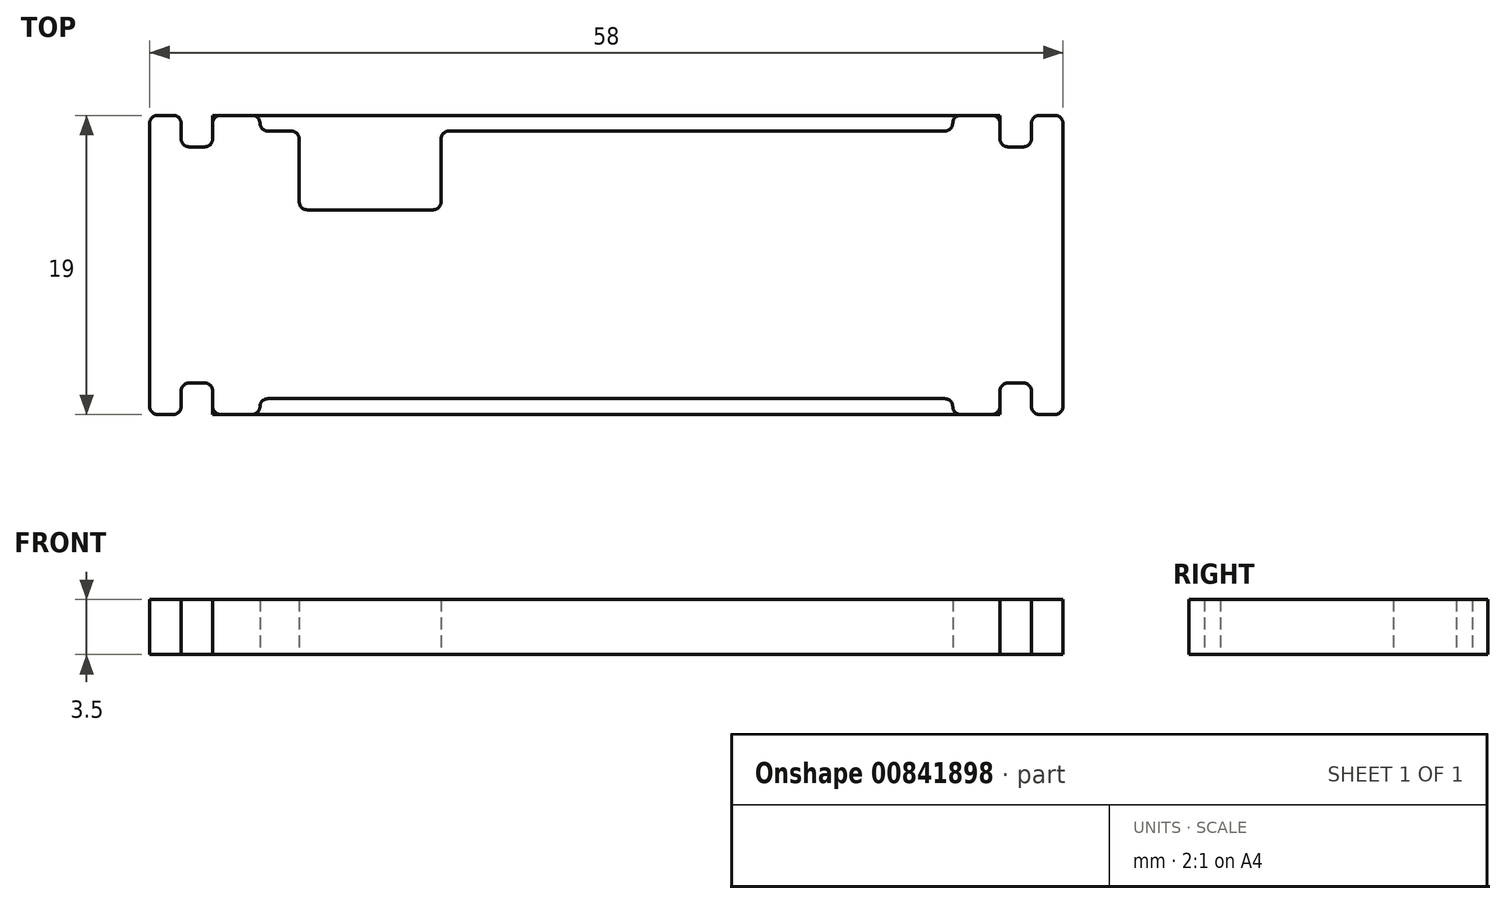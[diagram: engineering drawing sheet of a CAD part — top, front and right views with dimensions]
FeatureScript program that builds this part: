
annotation { "Feature Type Name" : "Feature", "Feature Type Description" : "" }
export const myFeature = defineFeature(function(context is Context, id is Id, definition is map)
    precondition{}
    {
        {
            var Q0;
            Q0=qCreatedBy(makeId("Top.planeOp"),FACE);
            var sketch = newSketch(context, id + "F0", { "sketchPlane" : qUnion([Q0])});
            skLineSegment(sketch, "E0", {"start": v(-28.5, 9.5) * mm, "end": v(-27.5, 9.5) * mm});
            skLineSegment(sketch, "E1", {"start": v(-27, 9) * mm, "end": v(-27, 8) * mm});
            skLineSegment(sketch, "E2", {"start": v(-26.5, 7.5) * mm, "end": v(-25.5, 7.5) * mm});
            skLineSegment(sketch, "E3", {"start": v(-25, 8) * mm, "end": v(-25, 9.5) * mm});
            skLineSegment(sketch, "E4", {"start": v(-25, 9.5) * mm, "end": v(0, 9.5) * mm});
            skLineSegment(sketch, "E5", {"start": v(-29, 9) * mm, "end": v(-29, 0) * mm});
            skLineSegment(sketch, "E6.MirrorCS", {"start": v(26.5, 7.5) * mm, "end": v(25.5, 7.5) * mm});
            skLineSegment(sketch, "E7.MirrorCS", {"start": v(28.5, 9.5) * mm, "end": v(27.5, 9.5) * mm});
            skLineSegment(sketch, "E8.MirrorCS", {"start": v(29, 9) * mm, "end": v(29, 0) * mm});
            skLineSegment(sketch, "E9.MirrorCS", {"start": v(25, 9.5) * mm, "end": v(0, 9.5) * mm});
            skLineSegment(sketch, "E10.MirrorCS", {"start": v(25, 8) * mm, "end": v(25, 9.5) * mm});
            skLineSegment(sketch, "E11.MirrorCS", {"start": v(27, 9) * mm, "end": v(27, 8) * mm});
            skLineSegment(sketch, "E12.MirrorCS", {"start": v(28.5, -9.5) * mm, "end": v(27.5, -9.5) * mm});
            skLineSegment(sketch, "E13.MirrorCS", {"start": v(-28.5, -9.5) * mm, "end": v(-27.5, -9.5) * mm});
            skLineSegment(sketch, "E14.MirrorCS", {"start": v(-26.5, -7.5) * mm, "end": v(-25.5, -7.5) * mm});
            skLineSegment(sketch, "E15.MirrorCS", {"start": v(26.5, -7.5) * mm, "end": v(25.5, -7.5) * mm});
            skLineSegment(sketch, "E16.MirrorCS", {"start": v(29, -9) * mm, "end": v(29, 0) * mm});
            skLineSegment(sketch, "E17.MirrorCS", {"start": v(-27, -9) * mm, "end": v(-27, -8) * mm});
            skLineSegment(sketch, "E18.MirrorCS", {"start": v(-29, -9) * mm, "end": v(-29, 0) * mm});
            skLineSegment(sketch, "E19.MirrorCS", {"start": v(27, -9) * mm, "end": v(27, -8) * mm});
            skLineSegment(sketch, "E20.MirrorCS", {"start": v(25, -8) * mm, "end": v(25, -9.5) * mm});
            skLineSegment(sketch, "E21.MirrorCS", {"start": v(25, -9.5) * mm, "end": v(0, -9.5) * mm});
            skLineSegment(sketch, "E22.MirrorCS", {"start": v(-25, -8) * mm, "end": v(-25, -9.5) * mm});
            skLineSegment(sketch, "E23.MirrorCS", {"start": v(-25, -9.5) * mm, "end": v(0, -9.5) * mm});
            skPoint(sketch, "E24.visualSharp", {"position": v(-29, 9.5) * mm});
            skArc(sketch, "E24.filletArc", {"start": v(-28.5, 9.5) * mm, "mid": v(-28.85, 9.35) * mm, "end": v(-29, 9) * mm});
            skPoint(sketch, "E25.visualSharp", {"position": v(-27, 9.5) * mm});
            skArc(sketch, "E25.filletArc", {"start": v(-27, 9) * mm, "mid": v(-27.15, 9.35) * mm, "end": v(-27.5, 9.5) * mm});
            skPoint(sketch, "E26.visualSharp", {"position": v(-27, 7.5) * mm});
            skArc(sketch, "E26.filletArc", {"start": v(-27, 8) * mm, "mid": v(-26.85, 7.65) * mm, "end": v(-26.5, 7.5) * mm});
            skPoint(sketch, "E27.visualSharp", {"position": v(-25, 7.5) * mm});
            skArc(sketch, "E27.filletArc", {"start": v(-25.5, 7.5) * mm, "mid": v(-25.15, 7.65) * mm, "end": v(-25, 8) * mm});
            skPoint(sketch, "E28.visualSharp", {"position": v(-29, -9.5) * mm});
            skArc(sketch, "E28.filletArc", {"start": v(-29, -9) * mm, "mid": v(-28.85, -9.35) * mm, "end": v(-28.5, -9.5) * mm});
            skPoint(sketch, "E29.visualSharp", {"position": v(-27, -9.5) * mm});
            skArc(sketch, "E29.filletArc", {"start": v(-27.5, -9.5) * mm, "mid": v(-27.15, -9.35) * mm, "end": v(-27, -9) * mm});
            skPoint(sketch, "E30.visualSharp", {"position": v(-27, -7.5) * mm});
            skArc(sketch, "E30.filletArc", {"start": v(-26.5, -7.5) * mm, "mid": v(-26.85, -7.65) * mm, "end": v(-27, -8) * mm});
            skPoint(sketch, "E31.visualSharp", {"position": v(-25, -7.5) * mm});
            skArc(sketch, "E31.filletArc", {"start": v(-25, -8) * mm, "mid": v(-25.15, -7.65) * mm, "end": v(-25.5, -7.5) * mm});
            skPoint(sketch, "E32.visualSharp", {"position": v(25, 7.5) * mm});
            skArc(sketch, "E32.filletArc", {"start": v(25, 8) * mm, "mid": v(25.15, 7.65) * mm, "end": v(25.5, 7.5) * mm});
            skPoint(sketch, "E33.visualSharp", {"position": v(27, 7.5) * mm});
            skArc(sketch, "E33.filletArc", {"start": v(26.5, 7.5) * mm, "mid": v(26.85, 7.65) * mm, "end": v(27, 8) * mm});
            skPoint(sketch, "E34.visualSharp", {"position": v(27, 9.5) * mm});
            skArc(sketch, "E34.filletArc", {"start": v(27.5, 9.5) * mm, "mid": v(27.15, 9.35) * mm, "end": v(27, 9) * mm});
            skPoint(sketch, "E35.visualSharp", {"position": v(29, 9.5) * mm});
            skArc(sketch, "E35.filletArc", {"start": v(29, 9) * mm, "mid": v(28.85, 9.35) * mm, "end": v(28.5, 9.5) * mm});
            skPoint(sketch, "E36.visualSharp", {"position": v(25, -7.5) * mm});
            skArc(sketch, "E36.filletArc", {"start": v(25.5, -7.5) * mm, "mid": v(25.15, -7.65) * mm, "end": v(25, -8) * mm});
            skPoint(sketch, "E37.visualSharp", {"position": v(27, -7.5) * mm});
            skArc(sketch, "E37.filletArc", {"start": v(27, -8) * mm, "mid": v(26.85, -7.65) * mm, "end": v(26.5, -7.5) * mm});
            skPoint(sketch, "E38.visualSharp", {"position": v(27, -9.5) * mm});
            skArc(sketch, "E38.filletArc", {"start": v(27, -9) * mm, "mid": v(27.15, -9.35) * mm, "end": v(27.5, -9.5) * mm});
            skPoint(sketch, "E39.visualSharp", {"position": v(29, -9.5) * mm});
            skArc(sketch, "E39.filletArc", {"start": v(28.5, -9.5) * mm, "mid": v(28.85, -9.35) * mm, "end": v(29, -9) * mm});
            skSolve(sketch);
        }
        {
            var Q0;
            Q0=qCreatedBy(makeId("Top.planeOp"),FACE);
            var sketch = newSketch(context, id + "F1", { "sketchPlane" : qUnion([Q0])});
            skLineSegment(sketch, "E40", {"start": v(-24.5, 9.5) * mm, "end": v(-22.5, 9.5) * mm});
            skLineSegment(sketch, "E41", {"start": v(-22, 9) * mm, "end": v(-22, 9) * mm});
            skLineSegment(sketch, "E42", {"start": v(-21.5, 8.5) * mm, "end": v(-20, 8.5) * mm});
            skLineSegment(sketch, "E43.MirrorCS", {"start": v(21.5, 8.5) * mm, "end": v(0, 8.5) * mm});
            skLineSegment(sketch, "E44.MirrorCS", {"start": v(22, 9) * mm, "end": v(22, 9) * mm});
            skLineSegment(sketch, "E45.MirrorCS", {"start": v(-24.5, -9.5) * mm, "end": v(-22.5, -9.5) * mm});
            skLineSegment(sketch, "E46.MirrorCS", {"start": v(-21.5, -8.5) * mm, "end": v(0, -8.5) * mm});
            skLineSegment(sketch, "E47.MirrorCS", {"start": v(21.5, -8.5) * mm, "end": v(0, -8.5) * mm});
            skLineSegment(sketch, "E48.MirrorCS", {"start": v(-22, -9) * mm, "end": v(-22, -9) * mm});
            skLineSegment(sketch, "E49.MirrorCS", {"start": v(22, -9) * mm, "end": v(22, -9) * mm});
            skPoint(sketch, "E50", {"position": v(-19.5, 8.5) * mm});
            skPoint(sketch, "E51", {"position": v(-10.5, 8.5) * mm});
            skLineSegment(sketch, "E52", {"start": v(-19.5, 8) * mm, "end": v(-19.5, 4) * mm});
            skLineSegment(sketch, "E53", {"start": v(-19, 3.5) * mm, "end": v(-11, 3.5) * mm});
            skLineSegment(sketch, "E54", {"start": v(-10.5, 4) * mm, "end": v(-10.5, 8) * mm});
            skLineSegment(sketch, "E55", {"start": v(-10, 8.5) * mm, "end": v(0, 8.5) * mm});
            skPoint(sketch, "E56.visualSharp", {"position": v(-19.5, 3.5) * mm});
            skArc(sketch, "E56.filletArc", {"start": v(-19.5, 4) * mm, "mid": v(-19.35, 3.65) * mm, "end": v(-19, 3.5) * mm});
            skArc(sketch, "E57.filletArc", {"start": v(-19.5, 8) * mm, "mid": v(-19.65, 8.35) * mm, "end": v(-20, 8.5) * mm});
            skPoint(sketch, "E58.visualSharp", {"position": v(-10.5, 3.5) * mm});
            skArc(sketch, "E58.filletArc", {"start": v(-11, 3.5) * mm, "mid": v(-10.65, 3.65) * mm, "end": v(-10.5, 4) * mm});
            skArc(sketch, "E59.filletArc", {"start": v(-10, 8.5) * mm, "mid": v(-10.35, 8.35) * mm, "end": v(-10.5, 8) * mm});
            skPoint(sketch, "E60.visualSharp", {"position": v(-22, 8.5) * mm});
            skArc(sketch, "E60.filletArc", {"start": v(-22, 9) * mm, "mid": v(-21.85, 8.65) * mm, "end": v(-21.5, 8.5) * mm});
            skPoint(sketch, "E61.visualSharp", {"position": v(-22, 9.5) * mm});
            skArc(sketch, "E61.filletArc", {"start": v(-22, 9) * mm, "mid": v(-22.15, 9.35) * mm, "end": v(-22.5, 9.5) * mm});
            skPoint(sketch, "E62.visualSharp", {"position": v(-22, -8.5) * mm});
            skArc(sketch, "E62.filletArc", {"start": v(-21.5, -8.5) * mm, "mid": v(-21.85, -8.65) * mm, "end": v(-22, -9) * mm});
            skPoint(sketch, "E63.visualSharp", {"position": v(22, -8.5) * mm});
            skArc(sketch, "E63.filletArc", {"start": v(22, -9) * mm, "mid": v(21.85, -8.65) * mm, "end": v(21.5, -8.5) * mm});
            skPoint(sketch, "E64.visualSharp", {"position": v(22, -9.5) * mm});
            skArc(sketch, "E64.filletArc", {"start": v(22, -9) * mm, "mid": v(22.15, -9.35) * mm, "end": v(22.5, -9.5) * mm});
            skPoint(sketch, "E65.visualSharp", {"position": v(-22, -9.5) * mm});
            skArc(sketch, "E65.filletArc", {"start": v(-22.5, -9.5) * mm, "mid": v(-22.15, -9.35) * mm, "end": v(-22, -9) * mm});
            skPoint(sketch, "E66.visualSharp", {"position": v(22, 8.5) * mm});
            skArc(sketch, "E66.filletArc", {"start": v(21.5, 8.5) * mm, "mid": v(21.85, 8.65) * mm, "end": v(22, 9) * mm});
            skLineSegment(sketch, "E67", {"start": v(22.5, 9.5) * mm, "end": v(24.5, 9.5) * mm});
            skPoint(sketch, "E68.visualSharp", {"position": v(22, 9.5) * mm});
            skArc(sketch, "E68.filletArc", {"start": v(22.5, 9.5) * mm, "mid": v(22.15, 9.35) * mm, "end": v(22, 9) * mm});
            skPoint(sketch, "E69.visualSharp", {"position": v(25, 9.5) * mm});
            skArc(sketch, "E69.filletArc", {"start": v(25, 9) * mm, "mid": v(24.85, 9.35) * mm, "end": v(24.5, 9.5) * mm});
            skLineSegment(sketch, "E70", {"start": v(25, 9) * mm, "end": v(25, 8) * mm});
            skLineSegment(sketch, "E71", {"start": v(25.5, 7.5) * mm, "end": v(26.5, 7.5) * mm});
            skLineSegment(sketch, "E72", {"start": v(27, 8) * mm, "end": v(27, 9) * mm});
            skLineSegment(sketch, "E73", {"start": v(27.5, 9.5) * mm, "end": v(28.5, 9.5) * mm});
            skLineSegment(sketch, "E74", {"start": v(29, 9) * mm, "end": v(29, 0) * mm});
            skPoint(sketch, "E75.visualSharp", {"position": v(25, 7.5) * mm});
            skArc(sketch, "E75.filletArc", {"start": v(25, 8) * mm, "mid": v(25.15, 7.65) * mm, "end": v(25.5, 7.5) * mm});
            skPoint(sketch, "E76.visualSharp", {"position": v(27, 7.5) * mm});
            skArc(sketch, "E76.filletArc", {"start": v(26.5, 7.5) * mm, "mid": v(26.85, 7.65) * mm, "end": v(27, 8) * mm});
            skPoint(sketch, "E77.visualSharp", {"position": v(27, 9.5) * mm});
            skArc(sketch, "E77.filletArc", {"start": v(27.5, 9.5) * mm, "mid": v(27.15, 9.35) * mm, "end": v(27, 9) * mm});
            skPoint(sketch, "E78.visualSharp", {"position": v(29, 9.5) * mm});
            skArc(sketch, "E78.filletArc", {"start": v(29, 9) * mm, "mid": v(28.85, 9.35) * mm, "end": v(28.5, 9.5) * mm});
            skLineSegment(sketch, "E79", {"start": v(29, 0) * mm, "end": v(29, -9) * mm});
            skLineSegment(sketch, "E80", {"start": v(28.5, -9.5) * mm, "end": v(27.5, -9.5) * mm});
            skLineSegment(sketch, "E81", {"start": v(27, -9) * mm, "end": v(27, -8) * mm});
            skLineSegment(sketch, "E82", {"start": v(26.5, -7.5) * mm, "end": v(25.5, -7.5) * mm});
            skLineSegment(sketch, "E83", {"start": v(25, -8) * mm, "end": v(25, -9) * mm});
            skLineSegment(sketch, "E84", {"start": v(22.5, -9.5) * mm, "end": v(24.5, -9.5) * mm});
            skPoint(sketch, "E85.visualSharp", {"position": v(29, -9.5) * mm});
            skArc(sketch, "E85.filletArc", {"start": v(28.5, -9.5) * mm, "mid": v(28.85, -9.35) * mm, "end": v(29, -9) * mm});
            skPoint(sketch, "E86.visualSharp", {"position": v(27, -9.5) * mm});
            skArc(sketch, "E86.filletArc", {"start": v(27, -9) * mm, "mid": v(27.15, -9.35) * mm, "end": v(27.5, -9.5) * mm});
            skPoint(sketch, "E87.visualSharp", {"position": v(27, -7.5) * mm});
            skArc(sketch, "E87.filletArc", {"start": v(27, -8) * mm, "mid": v(26.85, -7.65) * mm, "end": v(26.5, -7.5) * mm});
            skPoint(sketch, "E88.visualSharp", {"position": v(25, -7.5) * mm});
            skArc(sketch, "E88.filletArc", {"start": v(25.5, -7.5) * mm, "mid": v(25.15, -7.65) * mm, "end": v(25, -8) * mm});
            skPoint(sketch, "E89.visualSharp", {"position": v(25, -9.5) * mm});
            skArc(sketch, "E89.filletArc", {"start": v(24.5, -9.5) * mm, "mid": v(24.85, -9.35) * mm, "end": v(25, -9) * mm});
            skLineSegment(sketch, "E90", {"start": v(-25, -9) * mm, "end": v(-25, -8) * mm});
            skLineSegment(sketch, "E91", {"start": v(-25.5, -7.5) * mm, "end": v(-26.5, -7.5) * mm});
            skLineSegment(sketch, "E92", {"start": v(-27, -8) * mm, "end": v(-27, -9) * mm});
            skLineSegment(sketch, "E93", {"start": v(-27.5, -9.5) * mm, "end": v(-28.5, -9.5) * mm});
            skLineSegment(sketch, "E94", {"start": v(-29, -9) * mm, "end": v(-29, 0) * mm});
            skPoint(sketch, "E95.visualSharp", {"position": v(-25, -9.5) * mm});
            skArc(sketch, "E95.filletArc", {"start": v(-25, -9) * mm, "mid": v(-24.85, -9.35) * mm, "end": v(-24.5, -9.5) * mm});
            skPoint(sketch, "E96.visualSharp", {"position": v(-25, -7.5) * mm});
            skArc(sketch, "E96.filletArc", {"start": v(-25, -8) * mm, "mid": v(-25.15, -7.65) * mm, "end": v(-25.5, -7.5) * mm});
            skPoint(sketch, "E97.visualSharp", {"position": v(-27, -7.5) * mm});
            skArc(sketch, "E97.filletArc", {"start": v(-26.5, -7.5) * mm, "mid": v(-26.85, -7.65) * mm, "end": v(-27, -8) * mm});
            skPoint(sketch, "E98.visualSharp", {"position": v(-27, -9.5) * mm});
            skArc(sketch, "E98.filletArc", {"start": v(-27.5, -9.5) * mm, "mid": v(-27.15, -9.35) * mm, "end": v(-27, -9) * mm});
            skPoint(sketch, "E99.visualSharp", {"position": v(-29, -9.5) * mm});
            skArc(sketch, "E99.filletArc", {"start": v(-29, -9) * mm, "mid": v(-28.85, -9.35) * mm, "end": v(-28.5, -9.5) * mm});
            skLineSegment(sketch, "E100", {"start": v(-29, 0) * mm, "end": v(-29, 9) * mm});
            skLineSegment(sketch, "E101", {"start": v(-28.5, 9.5) * mm, "end": v(-27.5, 9.5) * mm});
            skLineSegment(sketch, "E102", {"start": v(-27, 8) * mm, "end": v(-27, 9) * mm});
            skLineSegment(sketch, "E103", {"start": v(-26.5, 7.5) * mm, "end": v(-25.5, 7.5) * mm});
            skLineSegment(sketch, "E104", {"start": v(-25, 8) * mm, "end": v(-25, 9) * mm});
            skPoint(sketch, "E105.visualSharp", {"position": v(-25, 9.5) * mm});
            skArc(sketch, "E105.filletArc", {"start": v(-24.5, 9.5) * mm, "mid": v(-24.85, 9.35) * mm, "end": v(-25, 9) * mm});
            skPoint(sketch, "E106.visualSharp", {"position": v(-25, 7.5) * mm});
            skArc(sketch, "E106.filletArc", {"start": v(-25.5, 7.5) * mm, "mid": v(-25.15, 7.65) * mm, "end": v(-25, 8) * mm});
            skPoint(sketch, "E107.visualSharp", {"position": v(-27, 7.5) * mm});
            skArc(sketch, "E107.filletArc", {"start": v(-27, 8) * mm, "mid": v(-26.85, 7.65) * mm, "end": v(-26.5, 7.5) * mm});
            skPoint(sketch, "E108.visualSharp", {"position": v(-27, 9.5) * mm});
            skArc(sketch, "E108.filletArc", {"start": v(-27, 9) * mm, "mid": v(-27.15, 9.35) * mm, "end": v(-27.5, 9.5) * mm});
            skPoint(sketch, "E109.visualSharp", {"position": v(-29, 9.5) * mm});
            skArc(sketch, "E109.filletArc", {"start": v(-28.5, 9.5) * mm, "mid": v(-28.85, 9.35) * mm, "end": v(-29, 9) * mm});
            skSolve(sketch);
        }
        {
            var Q0;
            Q0=makeQuery(id+"F1.imprint","IMPRINT",FACE,{"disambiguationData":[TD([[makeQuery(id+"F1.imprint","IMPRINT",EDGE,{"derivedFrom":sQuery(id+"F1.wireOp",EDGE,"E40")}),-1.0]])]});
            extrude(context, id + "F2", {"entities" : qUnion([Q0]), "depth" : 3.5 * mm, "offsetDistance" : 25 * mm});
        }
        {
            var Q0;
            Q0 = qSketchRegion(id + "F0", true);
            extrude(context, id + "F3", {"entities" : qUnion([Q0]), "depth" : 3.5 * mm, "offsetDistance" : 25 * mm});
        }
    });
